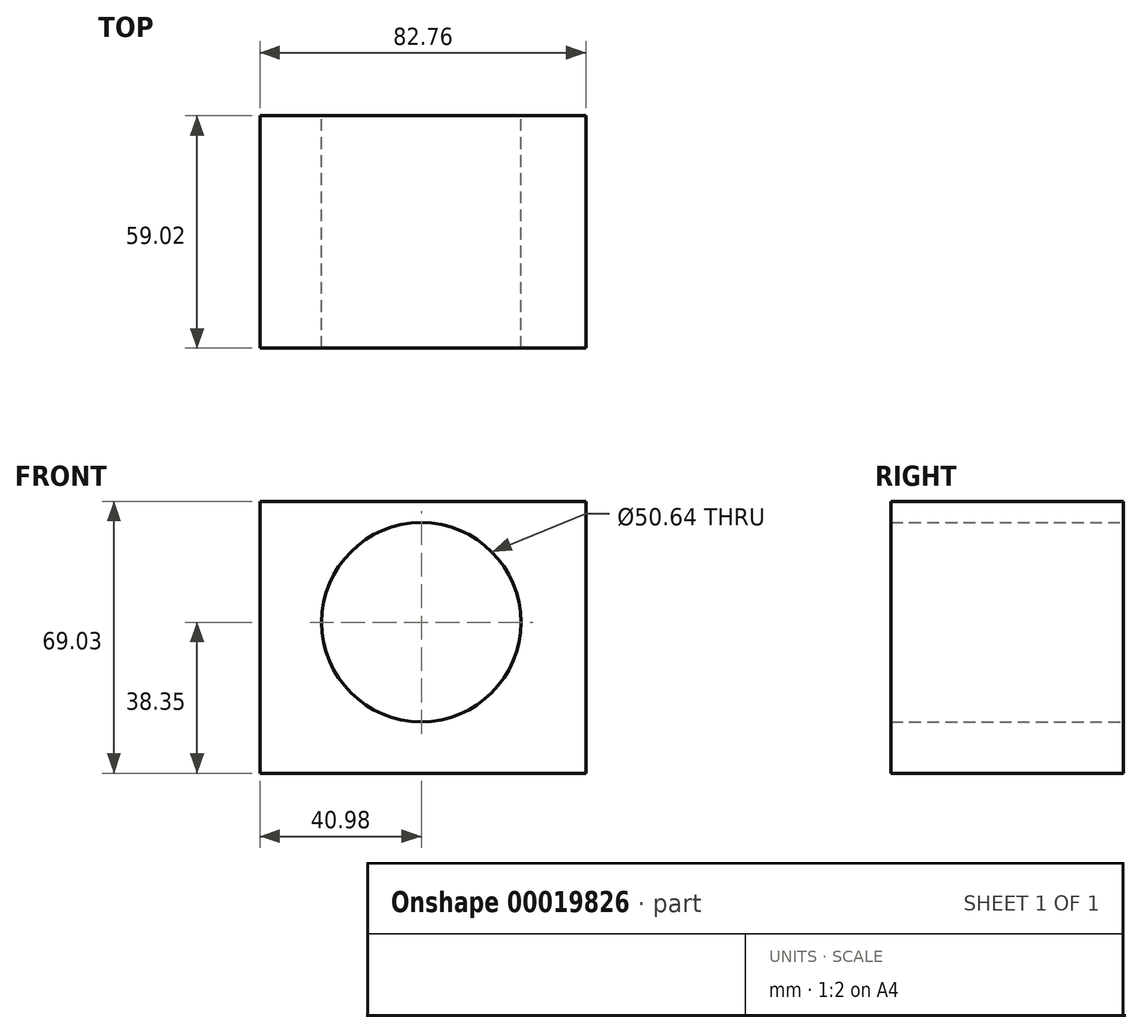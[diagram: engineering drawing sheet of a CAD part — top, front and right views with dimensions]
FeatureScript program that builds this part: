
annotation { "Feature Type Name" : "Feature", "Feature Type Description" : "" }
export const myFeature = defineFeature(function(context is Context, id is Id, definition is map)
    precondition{}
    {
        {
            var Q0;
            Q0=qCreatedBy(makeId("Front.planeOp"),FACE);
            var sketch = newSketch(context, id + "F0", { "sketchPlane" : qUnion([Q0])});
            skLineSegment(sketch, "E0.bottom", {"start": v(-40.98, 30.68) * mm, "end": v(41.78, 30.68) * mm});
            skLineSegment(sketch, "E0.top", {"start": v(-40.98, -38.35) * mm, "end": v(41.78, -38.35) * mm});
            skLineSegment(sketch, "E0.left", {"start": v(-40.98, 30.68) * mm, "end": v(-40.98, -38.35) * mm});
            skLineSegment(sketch, "E0.right", {"start": v(41.78, 30.68) * mm, "end": v(41.78, -38.35) * mm});
            skCircle(sketch, "E1", {"center": v(0, 0) * mm, "radius": 25.32 * mm});
            skSolve(sketch);
        }
        {
            var Q0;
            Q0=makeQuery(id+"F0.imprint","IMPRINT",FACE,{"disambiguationData":[TD([[makeQuery(id+"F0.imprint","IMPRINT",EDGE,{"derivedFrom":sQuery(id+"F0.wireOp",EDGE,"E0.bottom")}),-1.0]])]});
            extrude(context, id + "F1", {"entities" : qUnion([Q0]), "depth" : 59.02 * mm});
        }
    });
